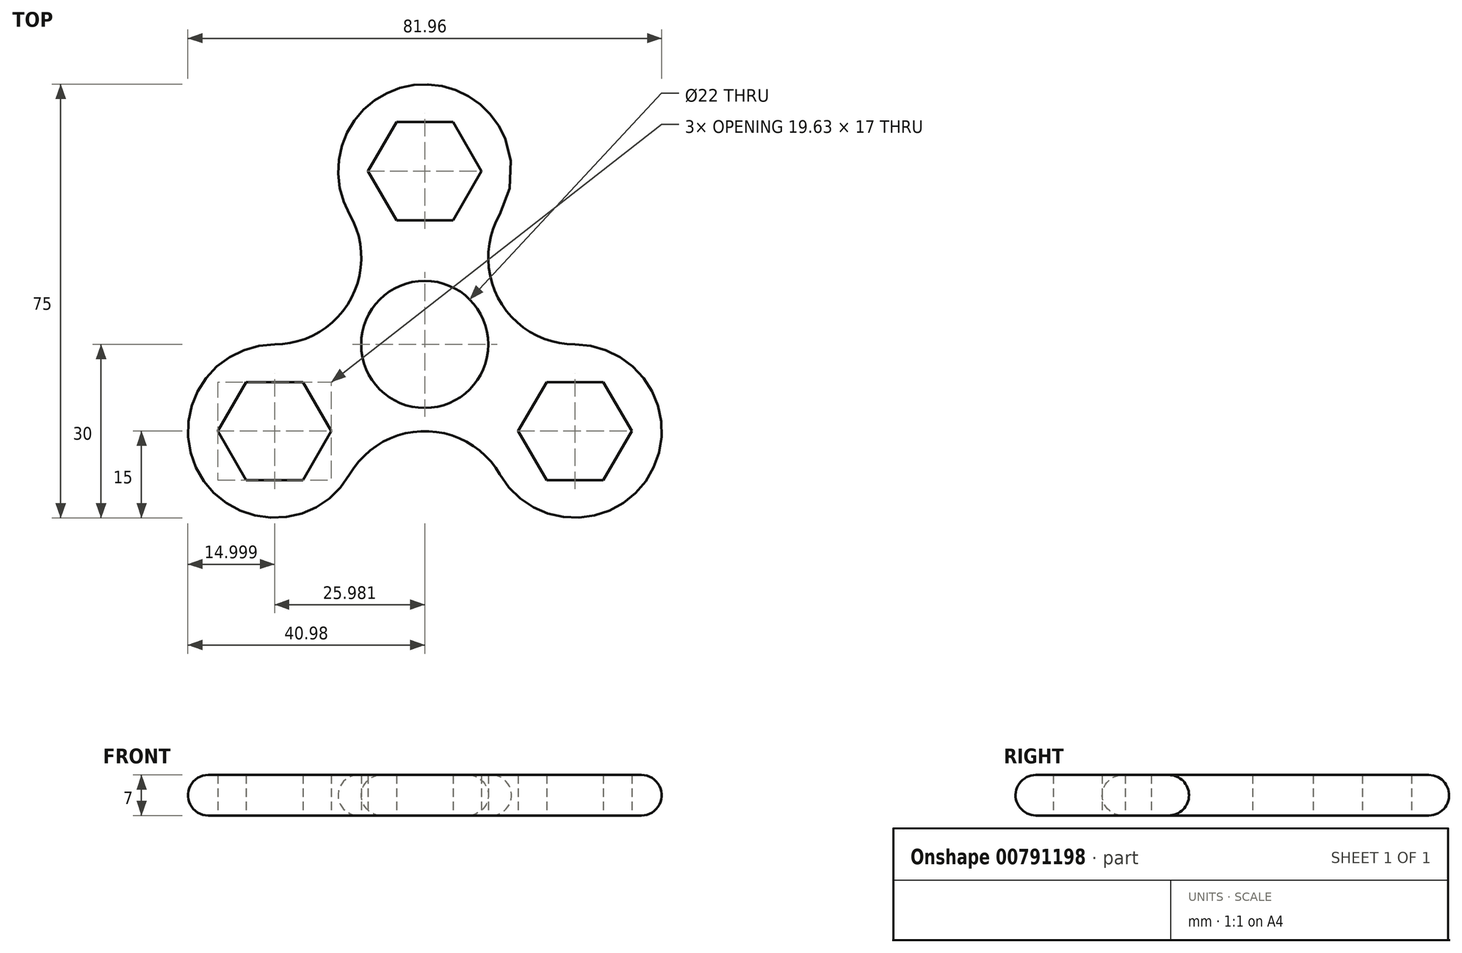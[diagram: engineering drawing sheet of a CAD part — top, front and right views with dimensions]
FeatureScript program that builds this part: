
annotation { "Feature Type Name" : "Feature", "Feature Type Description" : "" }
export const myFeature = defineFeature(function(context is Context, id is Id, definition is map)
    precondition{}
    {
        {
            var Q0;
            Q0=qCreatedBy(makeId("Top.planeOp"),FACE);
            var sketch = newSketch(context, id + "F0", { "sketchPlane" : qUnion([Q0])});
            skCircle(sketch, "E0", {"center": v(0, 0) * mm, "radius": 11 * mm});
            skCircle(sketch, "E1", {"center": v(0, 30) * mm, "radius": 15 * mm});
            skLineSegment(sketch, "E2", {"start": v(0, 30) * mm, "end": v(0, 0) * mm, "construction": true});
            skLineSegment(sketch, "E3", {"start": v(0, 0) * mm, "end": v(25.98, -15) * mm, "construction": true});
            skLineSegment(sketch, "E4", {"start": v(0, 0) * mm, "end": v(-25.98, -15) * mm, "construction": true});
            skCircle(sketch, "E5", {"center": v(-25.98, -15) * mm, "radius": 15 * mm});
            skCircle(sketch, "E6", {"center": v(25.98, -15) * mm, "radius": 15 * mm});
            skCircle(sketch, "E7.cCircle", {"center": v(-25.98, -15) * mm, "radius": 8.5 * mm, "construction": true});
            skLineSegment(sketch, "E7.0", {"start": v(-21.07, -6.5) * mm, "end": v(-16.17, -15) * mm});
            skLineSegment(sketch, "E7.1", {"start": v(-16.17, -15) * mm, "end": v(-21.07, -23.5) * mm});
            skLineSegment(sketch, "E7.2", {"start": v(-21.07, -23.5) * mm, "end": v(-30.89, -23.5) * mm});
            skLineSegment(sketch, "E7.3", {"start": v(-30.89, -23.5) * mm, "end": v(-35.8, -15) * mm});
            skLineSegment(sketch, "E7.4", {"start": v(-35.8, -15) * mm, "end": v(-30.89, -6.5) * mm});
            skLineSegment(sketch, "E7.5", {"start": v(-30.89, -6.5) * mm, "end": v(-21.07, -6.5) * mm});
            skPoint(sketch, "E7.0.midPoint", {"position": v(-18.62, -10.75) * mm});
            skCircle(sketch, "E8.cCircle", {"center": v(25.98, -15) * mm, "radius": 8.5 * mm, "construction": true});
            skLineSegment(sketch, "E8.0", {"start": v(16.17, -15) * mm, "end": v(21.07, -6.5) * mm});
            skLineSegment(sketch, "E8.1", {"start": v(21.07, -6.5) * mm, "end": v(30.89, -6.5) * mm});
            skLineSegment(sketch, "E8.2", {"start": v(30.89, -6.5) * mm, "end": v(35.8, -15) * mm});
            skLineSegment(sketch, "E8.3", {"start": v(35.8, -15) * mm, "end": v(30.89, -23.5) * mm});
            skLineSegment(sketch, "E8.4", {"start": v(30.89, -23.5) * mm, "end": v(21.07, -23.5) * mm});
            skLineSegment(sketch, "E8.5", {"start": v(21.07, -23.5) * mm, "end": v(16.17, -15) * mm});
            skPoint(sketch, "E8.0.midPoint", {"position": v(18.62, -10.75) * mm});
            skArc(sketch, "E9", {"start": v(-25.98, 0) * mm, "mid": v(-13, 7.5) * mm, "end": v(-13, 22.5) * mm});
            skArc(sketch, "E10", {"start": v(13, 22.5) * mm, "mid": v(13, 7.5) * mm, "end": v(25.98, 0) * mm});
            skArc(sketch, "E11", {"start": v(13, -22.5) * mm, "mid": v(0, -15) * mm, "end": v(-13, -22.5) * mm});
            skCircle(sketch, "E12.cCircle", {"center": v(0, 30) * mm, "radius": 8.5 * mm, "construction": true});
            skLineSegment(sketch, "E12.0", {"start": v(4.9, 21.5) * mm, "end": v(-4.9, 21.5) * mm});
            skLineSegment(sketch, "E12.1", {"start": v(-4.9, 21.5) * mm, "end": v(-9.81, 30) * mm});
            skLineSegment(sketch, "E12.2", {"start": v(-9.81, 30) * mm, "end": v(-4.9, 38.5) * mm});
            skLineSegment(sketch, "E12.3", {"start": v(-4.9, 38.5) * mm, "end": v(4.9, 38.5) * mm});
            skLineSegment(sketch, "E12.4", {"start": v(4.9, 38.5) * mm, "end": v(9.81, 30) * mm});
            skLineSegment(sketch, "E12.5", {"start": v(9.81, 30) * mm, "end": v(4.9, 21.5) * mm});
            skPoint(sketch, "E12.0.midPoint", {"position": v(0, 21.5) * mm});
            skCircle(sketch, "E13", {"center": v(0, 0) * mm, "radius": 15 * mm});
            skSolve(sketch);
        }
        {
            var Q0;
            Q0=makeQuery(id+"F0.imprint","IMPRINT",FACE,{"disambiguationData":[TD([[makeQuery(id+"F0.imprint","IMPRINT",EDGE,{"derivedFrom":sQuery(id+"F0.wireOp",EDGE,"E7.0")}),1.0]])]});
            var Q1;
            Q1=makeQuery(id+"F0.imprint","IMPRINT",FACE,{"disambiguationData":[TD([[makeQuery(id+"F0.imprint","IMPRINT",EDGE,{"derivedFrom":sQuery(id+"F0.wireOp",EDGE,"E0")}),-1.0]])]});
            var Q2;
            Q2=makeQuery(id+"F0.imprint","IMPRINT",FACE,{"disambiguationData":[TD([[makeQuery(id+"F0.imprint","IMPRINT",EDGE,{"derivedFrom":sQuery(id+"F0.wireOp",EDGE,"E12.0")}),1.0]])]});
            var Q3;
            Q3=makeQuery(id+"F0.imprint","IMPRINT",FACE,{"disambiguationData":[TD([[makeQuery(id+"F0.imprint","IMPRINT",EDGE,{"derivedFrom":sQuery(id+"F0.wireOp",EDGE,"E8.0")}),1.0]])]});
            var Q4;
            {var subQ0=sQuery(id+"F0.wireOp",EDGE,"E11");var subQ1=sQuery(id+"F0.wireOp",EDGE,"E5");var subQ2=makeQuery(id+"F0.imprint","INTERSECT",VERTEX,{"derivedFrom":[subQ1,subQ0]});Q4=makeQuery(id+"F0.imprint","IMPRINT",FACE,{"disambiguationData":[TD([[makeQuery(id+"F0.imprint","IMPRINT",EDGE,{"disambiguationData":[TD([[subQ2,-1.0]])],"derivedFrom":subQ1}),-1.0]])]});}
            var Q5;
            {var subQ0=sQuery(id+"F0.wireOp",EDGE,"E9");var subQ1=sQuery(id+"F0.wireOp",EDGE,"E5");var subQ2=makeQuery(id+"F0.imprint","INTERSECT",VERTEX,{"derivedFrom":[subQ1,subQ0]});Q5=makeQuery(id+"F0.imprint","IMPRINT",FACE,{"disambiguationData":[TD([[makeQuery(id+"F0.imprint","IMPRINT",EDGE,{"disambiguationData":[TD([[subQ2,1.0]])],"derivedFrom":subQ1}),-1.0]])]});}
            var Q6;
            {var subQ0=sQuery(id+"F0.wireOp",EDGE,"E9");var subQ1=sQuery(id+"F0.wireOp",EDGE,"E1");var subQ2=makeQuery(id+"F0.imprint","INTERSECT",VERTEX,{"derivedFrom":[subQ1,subQ0]});Q6=makeQuery(id+"F0.imprint","IMPRINT",FACE,{"disambiguationData":[TD([[makeQuery(id+"F0.imprint","IMPRINT",EDGE,{"disambiguationData":[TD([[subQ2,-1.0]])],"derivedFrom":subQ1}),-1.0]])]});}
            var Q7;
            {var subQ0=sQuery(id+"F0.wireOp",EDGE,"E10");var subQ1=sQuery(id+"F0.wireOp",EDGE,"E1");var subQ2=makeQuery(id+"F0.imprint","INTERSECT",VERTEX,{"derivedFrom":[subQ1,subQ0]});Q7=makeQuery(id+"F0.imprint","IMPRINT",FACE,{"disambiguationData":[TD([[makeQuery(id+"F0.imprint","IMPRINT",EDGE,{"disambiguationData":[TD([[subQ2,1.0]])],"derivedFrom":subQ1}),-1.0]])]});}
            var Q8;
            {var subQ0=sQuery(id+"F0.wireOp",EDGE,"E10");var subQ1=sQuery(id+"F0.wireOp",EDGE,"E6");var subQ2=makeQuery(id+"F0.imprint","INTERSECT",VERTEX,{"derivedFrom":[subQ1,subQ0]});Q8=makeQuery(id+"F0.imprint","IMPRINT",FACE,{"disambiguationData":[TD([[makeQuery(id+"F0.imprint","IMPRINT",EDGE,{"disambiguationData":[TD([[subQ2,-1.0]])],"derivedFrom":subQ1}),-1.0]])]});}
            var Q9;
            {var subQ0=sQuery(id+"F0.wireOp",EDGE,"E11");var subQ1=sQuery(id+"F0.wireOp",EDGE,"E6");var subQ2=makeQuery(id+"F0.imprint","INTERSECT",VERTEX,{"derivedFrom":[subQ1,subQ0]});Q9=makeQuery(id+"F0.imprint","IMPRINT",FACE,{"disambiguationData":[TD([[makeQuery(id+"F0.imprint","IMPRINT",EDGE,{"disambiguationData":[TD([[subQ2,1.0]])],"derivedFrom":subQ1}),-1.0]])]});}
            var Q10;
            {var subQ0=sQuery(id+"F0.wireOp",EDGE,"E13");var subQ1=sQuery(id+"F0.wireOp",EDGE,"E5");var subQ2=makeQuery(id+"F0.imprint","INTERSECT",VERTEX,{"disambiguationData":[OD(0.0)],"derivedFrom":[subQ1,subQ0]});Q10=makeQuery(id+"F0.imprint","IMPRINT",FACE,{"disambiguationData":[TD([[makeQuery(id+"F0.imprint","IMPRINT",EDGE,{"disambiguationData":[TD([[subQ2,1.0]])],"derivedFrom":subQ1}),1.0]])]});}
            var Q11;
            {var subQ0=sQuery(id+"F0.wireOp",EDGE,"E13");var subQ1=sQuery(id+"F0.wireOp",EDGE,"E1");var subQ2=makeQuery(id+"F0.imprint","INTERSECT",VERTEX,{"disambiguationData":[OD(0.0)],"derivedFrom":[subQ1,subQ0]});Q11=makeQuery(id+"F0.imprint","IMPRINT",FACE,{"disambiguationData":[TD([[makeQuery(id+"F0.imprint","IMPRINT",EDGE,{"disambiguationData":[TD([[subQ2,-1.0]])],"derivedFrom":subQ1}),1.0]])]});}
            var Q12;
            {var subQ0=sQuery(id+"F0.wireOp",EDGE,"E13");var subQ1=sQuery(id+"F0.wireOp",EDGE,"E6");var subQ2=makeQuery(id+"F0.imprint","INTERSECT",VERTEX,{"disambiguationData":[OD(0.0)],"derivedFrom":[subQ1,subQ0]});Q12=makeQuery(id+"F0.imprint","IMPRINT",FACE,{"disambiguationData":[TD([[makeQuery(id+"F0.imprint","IMPRINT",EDGE,{"disambiguationData":[TD([[subQ2,-1.0]])],"derivedFrom":subQ1}),1.0]])]});}
            extrude(context, id + "F1", {"entities" : qUnion([Q0, Q1, Q2, Q3, Q4, Q5, Q6, Q7, Q8, Q9, Q10, Q11, Q12]), "depth" : 7 * mm, "offsetDistance" : 25 * mm});
        }
        {
            var Q0;
            Q0=makeQuery(id+"F1.opExtrude","CAP_EDGE",EDGE,{"disambiguationData":[OSD([sQuery(id+"F0.wireOp",EDGE,"E11")])],"isStart":false});
            var Q1;
            Q1=makeQuery(id+"F1.opExtrude","CAP_EDGE",EDGE,{"disambiguationData":[OSD([sQuery(id+"F0.wireOp",EDGE,"E11")])],"isStart":true});
            fillet(context, id + "F2", {"entities" : qUnion([Q0, Q1]), "radius" : 3.5 * mm, "tangentPropagation" : true, "allowEdgeOverflow" : false});
        }
    });
